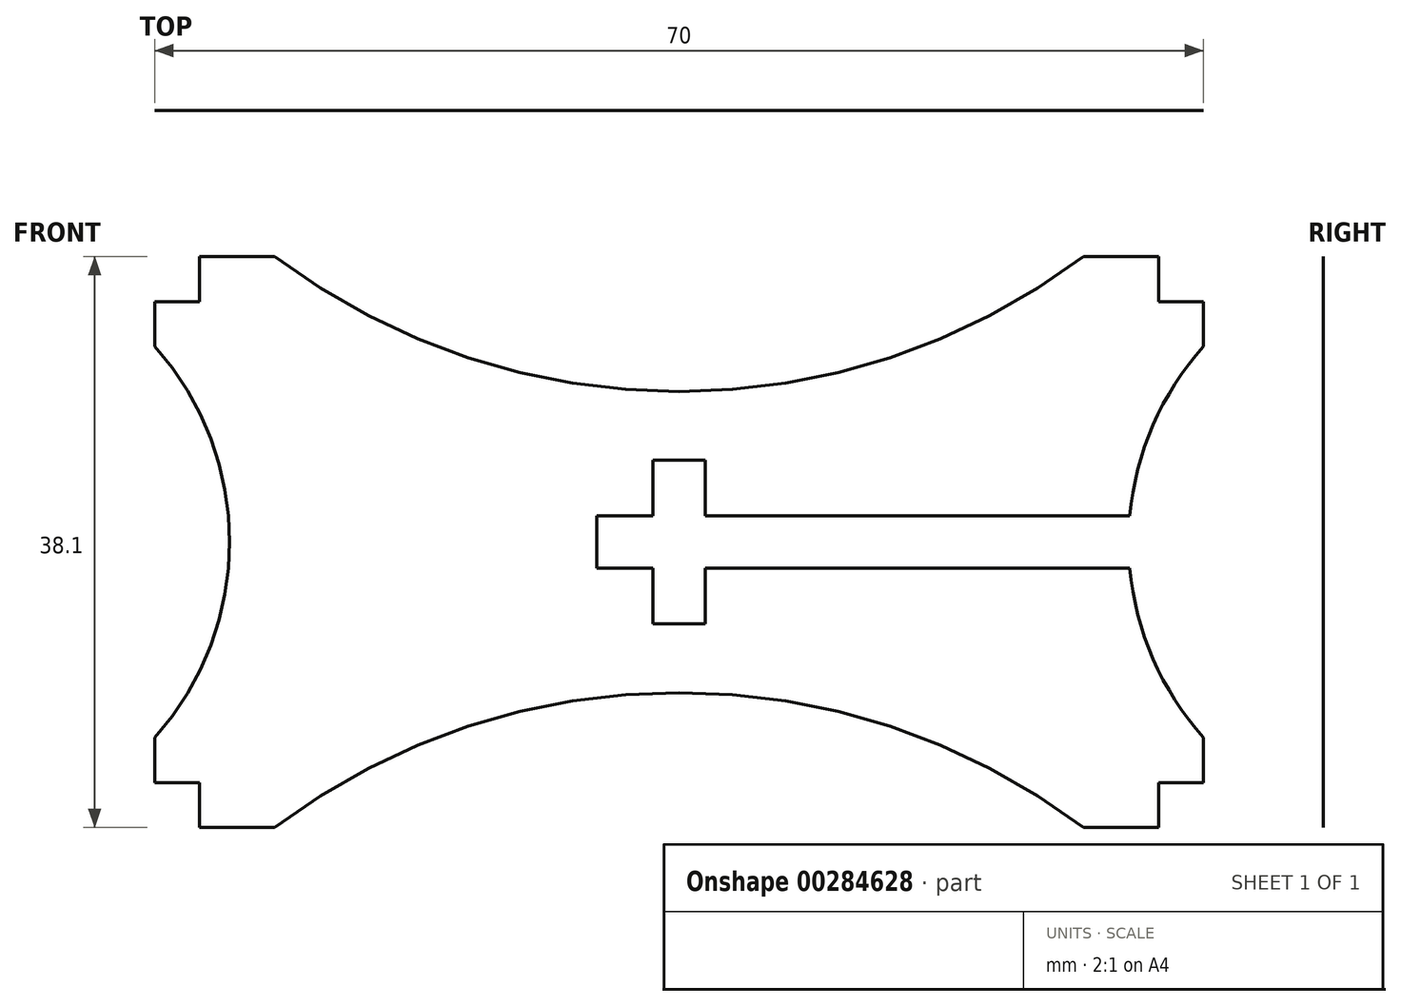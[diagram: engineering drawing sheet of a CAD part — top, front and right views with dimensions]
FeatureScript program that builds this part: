
annotation { "Feature Type Name" : "Feature", "Feature Type Description" : "" }
export const myFeature = defineFeature(function(context is Context, id is Id, definition is map)
    precondition{}
    {
        {
            var Q0;
            Q0=qCreatedBy(makeId("Front.planeOp"),FACE);
            var sketch = newSketch(context, id + "F0", { "sketchPlane" : qUnion([Q0])});
            skLineSegment(sketch, "E0.bottom", {"start": v(35, -19.05) * mm, "end": v(-35, -19.05) * mm});
            skLineSegment(sketch, "E0.top", {"start": v(35, 19.05) * mm, "end": v(-35, 19.05) * mm});
            skLineSegment(sketch, "E0.left", {"start": v(35, -19.05) * mm, "end": v(35, 19.05) * mm});
            skLineSegment(sketch, "E0.right", {"start": v(-35, -19.05) * mm, "end": v(-35, 19.05) * mm});
            skPoint(sketch, "E0.middle", {"position": v(0, 0) * mm});
            skLineSegment(sketch, "E1", {"start": v(-32, 19.05) * mm, "end": v(-32, -19.05) * mm});
            skLineSegment(sketch, "E2", {"start": v(32, 19.05) * mm, "end": v(32, -19.05) * mm});
            skLineSegment(sketch, "E3", {"start": v(-32, 16.05) * mm, "end": v(-35, 16.05) * mm});
            skLineSegment(sketch, "E4", {"start": v(32, 16.05) * mm, "end": v(35, 16.05) * mm});
            skLineSegment(sketch, "E5", {"start": v(-32, -16.05) * mm, "end": v(-35, -16.05) * mm});
            skLineSegment(sketch, "E6", {"start": v(32, -16.05) * mm, "end": v(35, -16.05) * mm});
            skArc(sketch, "E7", {"start": v(-35, -13.05) * mm, "mid": v(-30, 0) * mm, "end": v(-35, 13.05) * mm});
            skArc(sketch, "E8", {"start": v(35, 13.05) * mm, "mid": v(30, 0) * mm, "end": v(35, -13.05) * mm});
            skLineSegment(sketch, "E9", {"start": v(-5.5, 1.75) * mm, "end": v(-5.5, -1.75) * mm});
            skLineSegment(sketch, "E10", {"start": v(-30, 0) * mm, "end": v(30, 0) * mm});
            skArc(sketch, "E11", {"start": v(-27, 19.05) * mm, "mid": v(0, 10.05) * mm, "end": v(27, 19.05) * mm});
            skArc(sketch, "E12", {"start": v(27, -19.05) * mm, "mid": v(0, -10.05) * mm, "end": v(-27, -19.05) * mm});
            skLineSegment(sketch, "E13", {"start": v(-5.5, 1.75) * mm, "end": v(-1.75, 1.75) * mm});
            skLineSegment(sketch, "E14", {"start": v(-1.75, 1.75) * mm, "end": v(-1.75, 5.45) * mm});
            skLineSegment(sketch, "E15", {"start": v(-1.75, 5.45) * mm, "end": v(1.75, 5.45) * mm});
            skLineSegment(sketch, "E16", {"start": v(1.75, 5.45) * mm, "end": v(1.75, 1.75) * mm});
            skLineSegment(sketch, "E17", {"start": v(1.75, 1.75) * mm, "end": v(30.08, 1.75) * mm});
            skLineSegment(sketch, "E18", {"start": v(-5.5, -1.75) * mm, "end": v(-1.75, -1.75) * mm});
            skLineSegment(sketch, "E19", {"start": v(-1.75, -1.75) * mm, "end": v(-1.75, -5.45) * mm});
            skLineSegment(sketch, "E20", {"start": v(-1.75, -5.45) * mm, "end": v(1.75, -5.45) * mm});
            skLineSegment(sketch, "E21", {"start": v(1.75, -5.45) * mm, "end": v(1.75, -1.75) * mm});
            skLineSegment(sketch, "E22", {"start": v(1.75, -1.75) * mm, "end": v(30.08, -1.75) * mm});
            skPoint(sketch, "E23", {"position": v(0, -5.45) * mm});
            skSolve(sketch);
        }
        {
            var Q0;
            {var subQ0=sQuery(id+"F0.wireOp",EDGE,"E6");Q0=makeQuery(id+"F0.imprint","IMPRINT",FACE,{"disambiguationData":[TD([[makeQuery(id+"F0.imprint","IMPRINT",EDGE,{"derivedFrom":subQ0}),1.0]])]});}
            var Q1;
            {var subQ0=sQuery(id+"F0.wireOp",EDGE,"E4");Q1=makeQuery(id+"F0.imprint","IMPRINT",FACE,{"disambiguationData":[TD([[makeQuery(id+"F0.imprint","IMPRINT",EDGE,{"derivedFrom":subQ0}),-1.0]])]});}
            var Q2;
            {var subQ0=sQuery(id+"F0.wireOp",EDGE,"E5");Q2=makeQuery(id+"F0.imprint","IMPRINT",FACE,{"disambiguationData":[TD([[makeQuery(id+"F0.imprint","IMPRINT",EDGE,{"derivedFrom":subQ0}),-1.0]])]});}
            var Q3;
            {var subQ9=sQuery(id+"F0.wireOp",EDGE,"E12");Q3=makeQuery(id+"F0.imprint","IMPRINT",FACE,{"disambiguationData":[TD([[makeQuery(id+"F0.imprint","IMPRINT",EDGE,{"derivedFrom":subQ9}),-1.0]])]});}
            var Q4;
            {var subQ15=sQuery(id+"F0.wireOp",EDGE,"E11");Q4=makeQuery(id+"F0.imprint","IMPRINT",FACE,{"disambiguationData":[TD([[makeQuery(id+"F0.imprint","IMPRINT",EDGE,{"derivedFrom":subQ15}),-1.0]])]});}
            var Q5;
            {var subQ0=sQuery(id+"F0.wireOp",EDGE,"E3");Q5=makeQuery(id+"F0.imprint","IMPRINT",FACE,{"disambiguationData":[TD([[makeQuery(id+"F0.imprint","IMPRINT",EDGE,{"derivedFrom":subQ0}),1.0]])]});}
            extrude(context, id + "F1", {"entities" : qUnion([Q0, Q1, Q2, Q3, Q4, Q5]), "depth" : 1 / 203.2 * mm});
        }
    });
